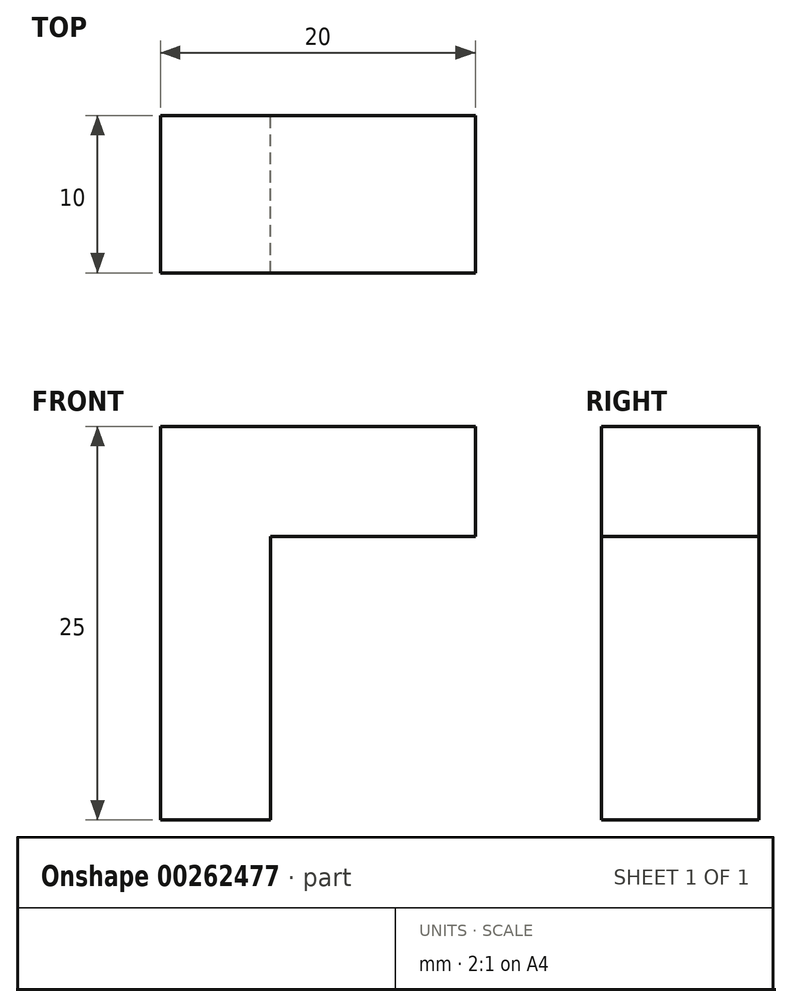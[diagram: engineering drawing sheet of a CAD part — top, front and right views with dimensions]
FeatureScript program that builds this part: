
annotation { "Feature Type Name" : "Feature", "Feature Type Description" : "" }
export const myFeature = defineFeature(function(context is Context, id is Id, definition is map)
    precondition{}
    {
        {
            var Q0;
            Q0=qCreatedBy(makeId("Front.planeOp"),FACE);
            var sketch = newSketch(context, id + "F0", { "sketchPlane" : qUnion([Q0])});
            skLineSegment(sketch, "E0", {"start": v(0, 0) * mm, "end": v(0, 25) * mm});
            skLineSegment(sketch, "E1", {"start": v(0, 25) * mm, "end": v(20, 25) * mm});
            skLineSegment(sketch, "E2", {"start": v(20, 25) * mm, "end": v(20, 18) * mm});
            skLineSegment(sketch, "E3", {"start": v(20, 18) * mm, "end": v(7, 18) * mm});
            skLineSegment(sketch, "E4", {"start": v(7, 18) * mm, "end": v(7, 0) * mm});
            skLineSegment(sketch, "E5", {"start": v(7, 0) * mm, "end": v(0, 0) * mm});
            skSolve(sketch);
        }
        {
            var Q0;
            Q0=makeQuery(id+"F0.imprint","IMPRINT",FACE,{"disambiguationData":[TD([[makeQuery(id+"F0.imprint","IMPRINT",EDGE,{"derivedFrom":sQuery(id+"F0.wireOp",EDGE,"E0")}),-1.0]])]});
            extrude(context, id + "F1", {"entities" : qUnion([Q0]), "depth" : 10 * mm});
        }
    });
